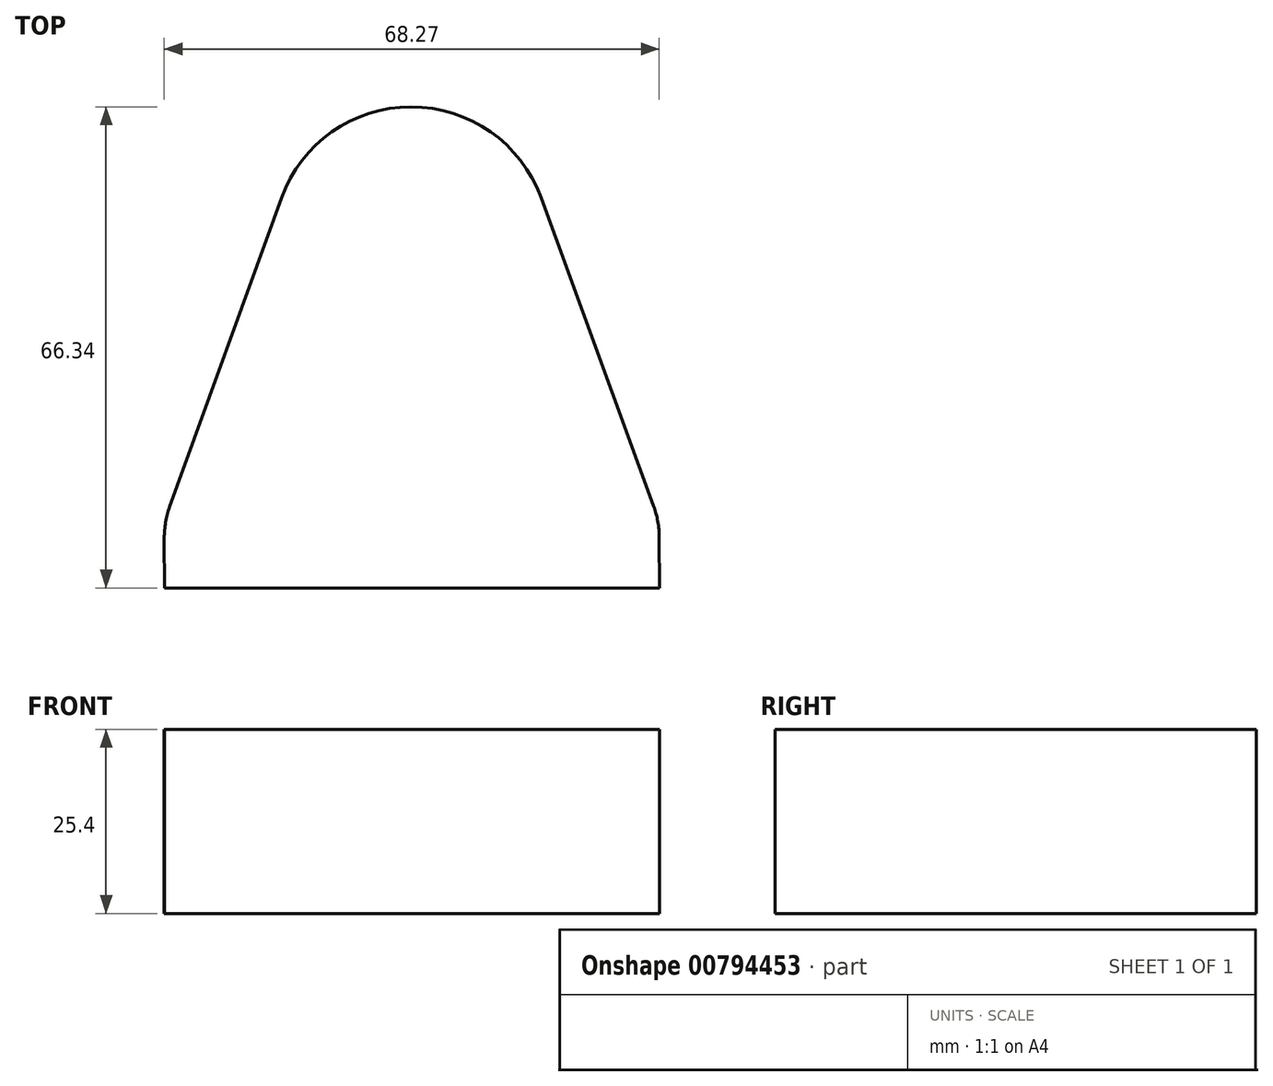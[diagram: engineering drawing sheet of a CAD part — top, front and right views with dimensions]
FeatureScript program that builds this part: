
annotation { "Feature Type Name" : "Feature", "Feature Type Description" : "" }
export const myFeature = defineFeature(function(context is Context, id is Id, definition is map)
    precondition{}
    {
        {
            var Q0;
            Q0=qCreatedBy(makeId("Top.planeOp"),FACE);
            var sketch = newSketch(context, id + "F0", { "sketchPlane" : qUnion([Q0])});
            skArc(sketch, "E0", {"start": v(17.9, 6.53) * mm, "mid": v(-0.03, 19.05) * mm, "end": v(-17.91, 6.48) * mm});
            skLineSegment(sketch, "E1.left", {"start": v(-34.07, -40.44) * mm, "end": v(-33.82, -197.66) * mm});
            skLineSegment(sketch, "E1.right", {"start": v(34.2, -40.34) * mm, "end": v(34.44, -197.56) * mm});
            skLineSegment(sketch, "E2", {"start": v(33.42, -36) * mm, "end": v(17.9, 6.53) * mm});
            skLineSegment(sketch, "E3", {"start": v(-33.31, -36.1) * mm, "end": v(-17.91, 6.48) * mm});
            skLineSegment(sketch, "E4", {"start": v(-33.82, -197.66) * mm, "end": v(34.44, -197.56) * mm});
            skLineSegment(sketch, "E5", {"start": v(-34.07, -38.2) * mm, "end": v(34.2, -38.1) * mm, "construction": true});
            skPoint(sketch, "E6.visualSharp", {"position": v(34.2, -38.1) * mm});
            skArc(sketch, "E6.filletArc", {"start": v(34.2, -40.34) * mm, "mid": v(34, -38.13) * mm, "end": v(33.42, -36) * mm});
            skPoint(sketch, "E7.visualSharp", {"position": v(-34.07, -38.2) * mm});
            skArc(sketch, "E7.filletArc", {"start": v(-33.31, -36.1) * mm, "mid": v(-33.88, -38.24) * mm, "end": v(-34.07, -40.44) * mm});
            skLineSegment(sketch, "E8", {"start": v(-17.91, 6.48) * mm, "end": v(17.9, 6.53) * mm, "construction": true});
            skSolve(sketch);
        }
        {
            var Q0;
            Q0=makeQuery(id+"F0.imprint","IMPRINT",FACE,{"disambiguationData":[TD([[makeQuery(id+"F0.imprint","IMPRINT",EDGE,{"derivedFrom":sQuery(id+"F0.wireOp",EDGE,"E0")}),1.0]])]});
            extrude(context, id + "F1", {"entities" : qUnion([Q0]), "depth" : 25.4 * mm, "offsetDistance" : 25.4 * mm});
        }
        {
            var Q0;
            Q0=makeQuery(id+"F1.opExtrude","CAP_FACE",FACE,{"disambiguationData":[OSD([sQuery(id+"F0.wireOp",EDGE,"E0"),sQuery(id+"F0.wireOp",EDGE,"E1.left"),sQuery(id+"F0.wireOp",EDGE,"E1.right"),sQuery(id+"F0.wireOp",EDGE,"E2"),sQuery(id+"F0.wireOp",EDGE,"E3"),sQuery(id+"F0.wireOp",EDGE,"E4"),sQuery(id+"F0.wireOp",EDGE,"4608d917-8397-4fe6-9836-2379d33c07fc.filletArc"),sQuery(id+"F0.wireOp",EDGE,"fa2758ce-228f-42ff-8725-96282f76b5d2.filletArc")])],"isStart":true});
            var sketch = newSketch(context, id + "F2", { "sketchPlane" : qUnion([Q0])});
            skLineSegment(sketch, "E9.bottom", {"start": v(108.32, 47.3) * mm, "end": v(-125.47, 47.3) * mm});
            skLineSegment(sketch, "E9.top", {"start": v(108.32, 236.16) * mm, "end": v(-125.47, 236.16) * mm});
            skLineSegment(sketch, "E9.left", {"start": v(108.32, 47.3) * mm, "end": v(108.32, 236.16) * mm});
            skLineSegment(sketch, "E9.right", {"start": v(-125.47, 47.3) * mm, "end": v(-125.47, 236.16) * mm});
            skSolve(sketch);
        }
        {
            var Q0;
            Q0 = qSketchRegion(id + "F2", true);
            extrude(context, id + "F3", {"entities" : qUnion([Q0]), "operationType" : NewBodyOperationType.REMOVE, "oppositeDirection" : true, "depth" : 91.95 * mm, "offsetDistance" : 25.4 * mm});
        }
    });
